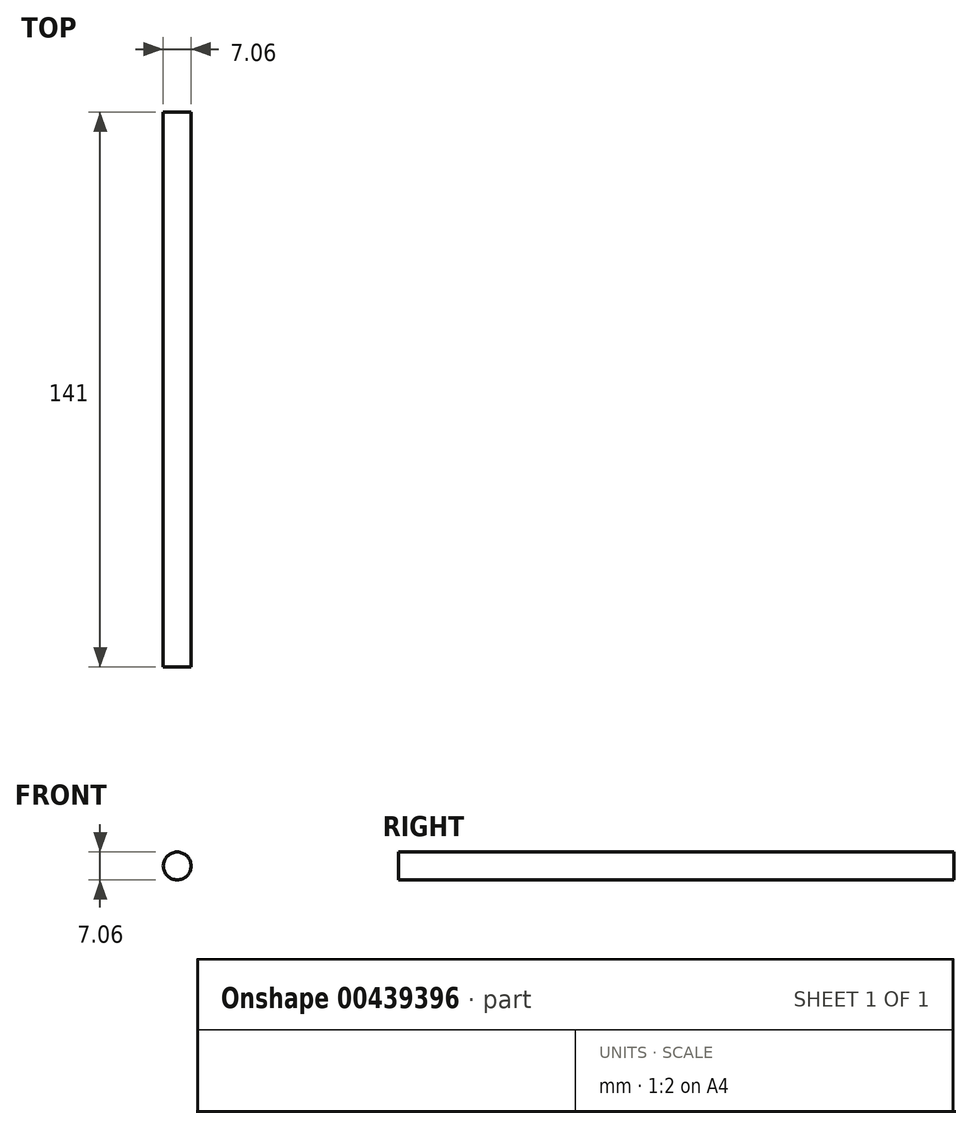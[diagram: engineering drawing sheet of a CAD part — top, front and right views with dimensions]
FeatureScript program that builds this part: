
annotation { "Feature Type Name" : "Feature", "Feature Type Description" : "" }
export const myFeature = defineFeature(function(context is Context, id is Id, definition is map)
    precondition{}
    {
        {
            var Q0;
            Q0=qCreatedBy(makeId("Front.planeOp"),FACE);
            var sketch = newSketch(context, id + "F0", { "sketchPlane" : qUnion([Q0])});
            skCircle(sketch, "E0", {"center": v(0, 0) * mm, "radius": 3.53 * mm});
            skSolve(sketch);
        }
        {
            var Q0;
            Q0 = qSketchRegion(id + "F0", true);
            extrude(context, id + "F1", {"entities" : qUnion([Q0]), "oppositeDirection" : true, "depth" : 141 * mm});
        }
    });
